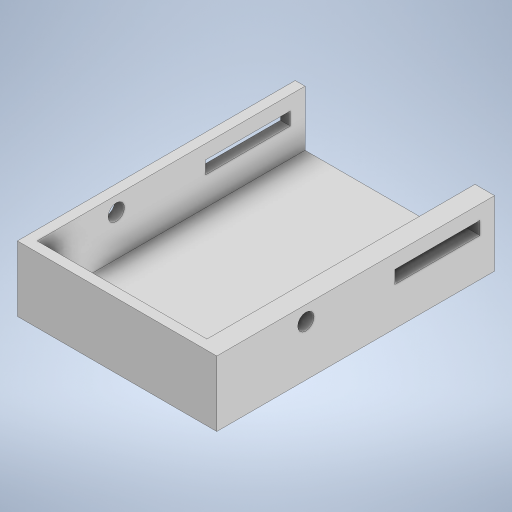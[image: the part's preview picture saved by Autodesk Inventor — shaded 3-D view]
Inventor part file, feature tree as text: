
AUTODESK INVENTOR PART (.ipt)
format: ipt  version: 2023 (Build 270158000, 158)  size: 266,240 bytes
history: native  units: in
note: dims shown in document units (in); Inventor stores cm internally (conversion verified against a paired STEP export)
features: sketch x6, extrude x5, shell x1
ambient origin geometry x8: Origin, YZ Plane, XZ Plane, XY Plane, X Axis, Y Axis, Z Axis, Center Point
bodies: Solid1 (feature_tree)
feature tree (12):
  extrude  "Extrusion1"  Depth=3.3465in
  shell  "Shell1"  Thickness=0.7874in
  sketch  "Sketch4"  dims[d4=0.1181in d17=0.3937in d18=0.0in]
  extrude  "Extrusion3"  Depth=0.3937in TaperAngle=0.0deg
  sketch  "Sketch6"  dims[d21=0.1772in d25=0.1181in d26=0.0in]
  extrude  "Extrusion5"  Depth=0.1575in
  extrude  "Extrusion6"  Depth=0.1181in TaperAngle=0.0deg
  extrude  "Extrusion7"  Depth=0.1969in
  sketch  "Sketch2"  dims[d0=2.2835in d1=3.3465in d2=0.7874in d3=0.0in]
  sketch  "Sketch5"  dims[d19=1.0236in d20=0.1575in]
  sketch  "Sketch7"  dims[d27=0.0in d28=0.0in d29=0.1969in]
  sketch  "Sketch8"  dims[d30=0.0in d31=0.0in d32=0.1772in d34=0.4606in d35=2.1457in d36=1.0728in d13=0.0197in d14=0.0344in d15=0.0197in d16=0.0344in d33=0.0344in]
